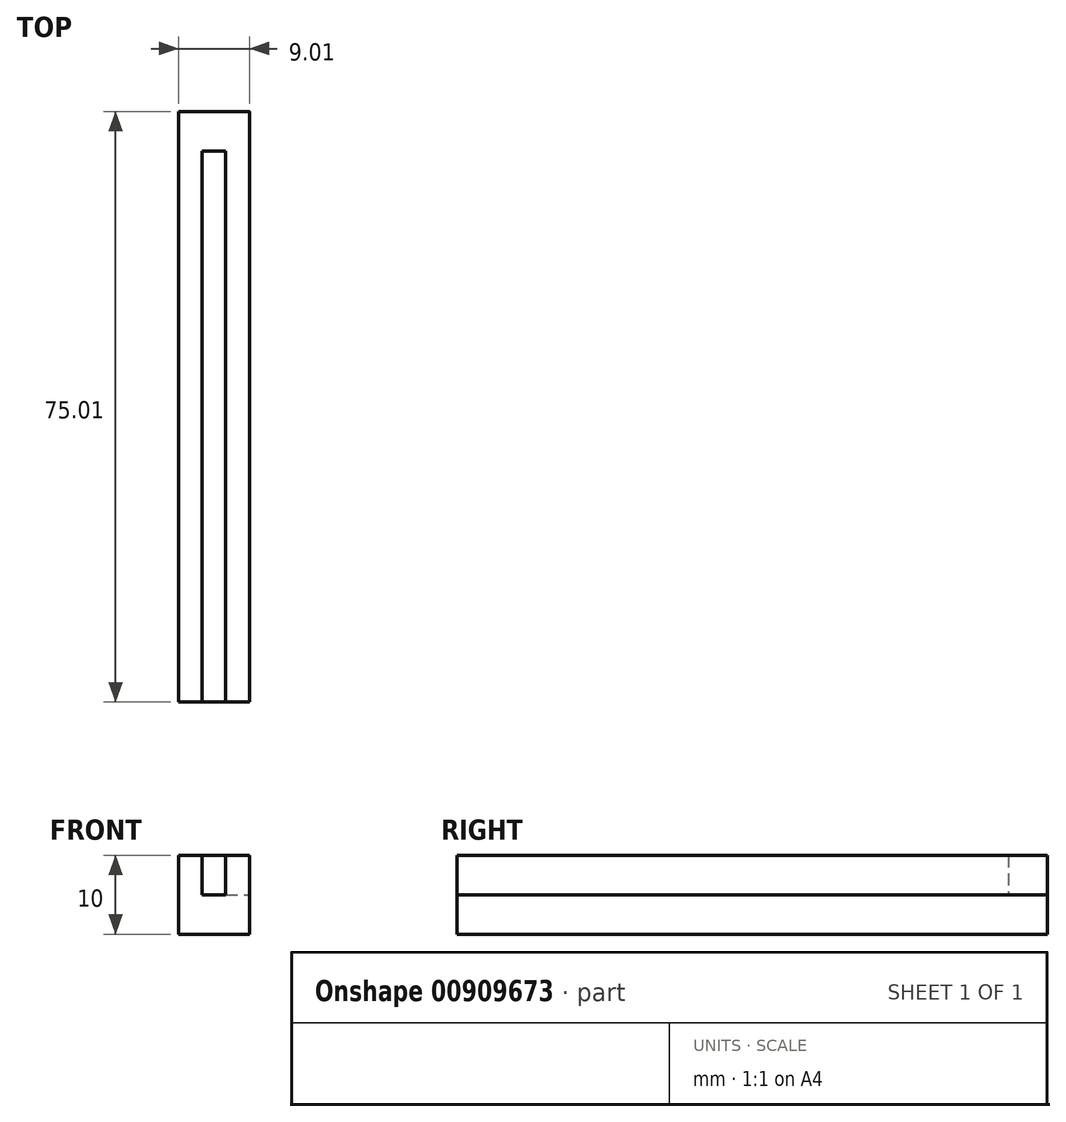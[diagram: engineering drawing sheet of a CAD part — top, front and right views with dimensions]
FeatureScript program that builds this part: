
annotation { "Feature Type Name" : "Feature", "Feature Type Description" : "" }
export const myFeature = defineFeature(function(context is Context, id is Id, definition is map)
    precondition{}
    {
        {
            var Q0;
            Q0=qCreatedBy(makeId("Top.planeOp"),FACE);
            var sketch = newSketch(context, id + "F0", { "sketchPlane" : qUnion([Q0])});
            skLineSegment(sketch, "E0.bottom", {"start": v(-4.5, 37.5) * mm, "end": v(4.5, 37.5) * mm});
            skLineSegment(sketch, "E0.top", {"start": v(-4.5, -37.5) * mm, "end": v(4.5, -37.5) * mm});
            skLineSegment(sketch, "E0.left", {"start": v(-4.5, 37.5) * mm, "end": v(-4.5, -37.5) * mm});
            skLineSegment(sketch, "E0.right", {"start": v(4.5, 37.5) * mm, "end": v(4.5, -37.5) * mm});
            skPoint(sketch, "E0.middle", {"position": v(0, 0) * mm});
            skSolve(sketch);
        }
        {
            var Q0;
            Q0=qCreatedBy(makeId("Top.planeOp"),FACE);
            var sketch = newSketch(context, id + "F1", { "sketchPlane" : qUnion([Q0])});
            skLineSegment(sketch, "E1.bottom", {"start": v(-4.51, 37.5) * mm, "end": v(-1.51, 37.5) * mm});
            skLineSegment(sketch, "E1.top", {"start": v(-4.51, -37.5) * mm, "end": v(-1.51, -37.5) * mm});
            skLineSegment(sketch, "E1.left", {"start": v(-4.51, 37.5) * mm, "end": v(-4.51, -37.5) * mm});
            skLineSegment(sketch, "E1.right", {"start": v(-1.51, 32.5) * mm, "end": v(-1.51, -37.5) * mm});
            skLineSegment(sketch, "E2.bottom", {"start": v(4.49, 37.5) * mm, "end": v(1.49, 37.5) * mm});
            skLineSegment(sketch, "E2.top", {"start": v(4.49, -37.5) * mm, "end": v(1.49, -37.5) * mm});
            skLineSegment(sketch, "E2.left", {"start": v(4.49, 37.5) * mm, "end": v(4.49, -37.5) * mm});
            skLineSegment(sketch, "E2.right", {"start": v(1.49, 37.5) * mm, "end": v(1.49, 37.5) * mm});
            skLineSegment(sketch, "E3.bottom", {"start": v(-4.51, 37.5) * mm, "end": v(4.49, 37.5) * mm});
            skLineSegment(sketch, "E3.top", {"start": v(-1.51, 32.5) * mm, "end": v(1.49, 32.5) * mm});
            skLineSegment(sketch, "E3.left", {"start": v(-4.51, 37.5) * mm, "end": v(-4.51, 32.5) * mm});
            skLineSegment(sketch, "E3.right", {"start": v(4.49, 37.5) * mm, "end": v(4.49, 32.5) * mm});
            skLineSegment(sketch, "E4.trimOffspring", {"start": v(1.49, 32.5) * mm, "end": v(1.49, -37.5) * mm});
            skSolve(sketch);
        }
        {
            var Q0;
            Q0 = qSketchRegion(id + "F0", true);
            extrude(context, id + "F2", {"entities" : qUnion([Q0]), "oppositeDirection" : true, "depth" : 5 * mm, "offsetDistance" : 25 * mm});
        }
        {
            var Q0;
            Q0 = qSketchRegion(id + "F1", true);
            extrude(context, id + "F3", {"entities" : qUnion([Q0]), "operationType" : NewBodyOperationType.ADD, "depth" : 5 * mm, "offsetDistance" : 25 * mm});
        }
    });
